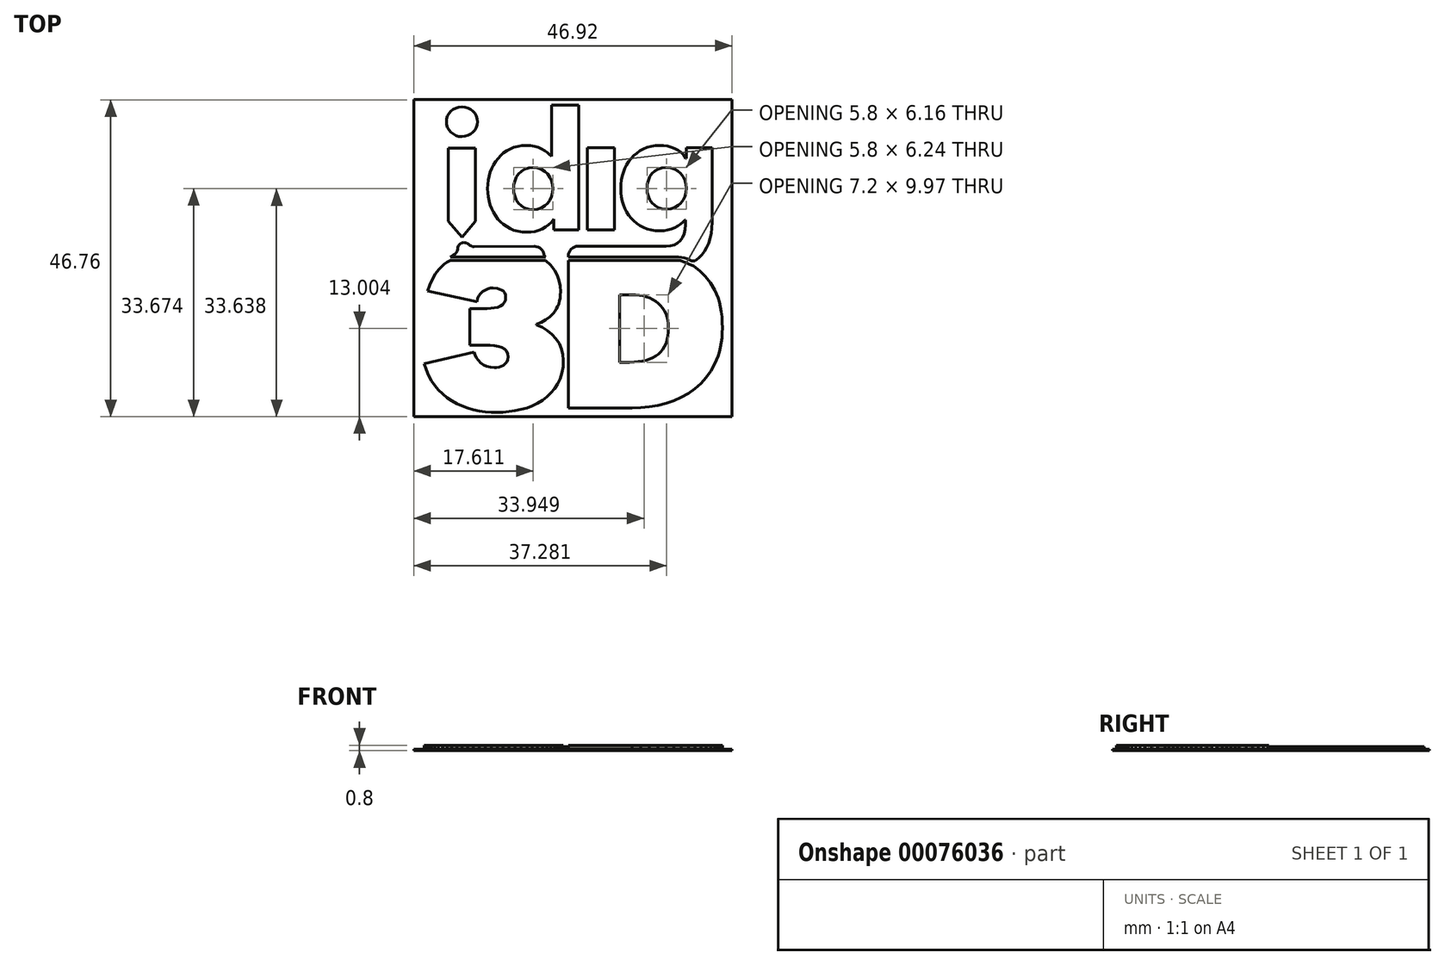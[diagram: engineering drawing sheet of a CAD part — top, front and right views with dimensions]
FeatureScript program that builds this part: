
annotation { "Feature Type Name" : "Feature", "Feature Type Description" : "" }
export const myFeature = defineFeature(function(context is Context, id is Id, definition is map)
    precondition{}
    {
        {
            var Q0;
            Q0=qCreatedBy(makeId("Top.planeOp"),FACE);
            var sketch = newSketch(context, id + "F0", { "sketchPlane" : qUnion([Q0])});
            skLineSegment(sketch, "E0", {"start": v(-3.12, 22.59) * mm, "end": v(0.88, 22.59) * mm});
            skLineSegment(sketch, "E1", {"start": v(0.88, 22.59) * mm, "end": v(0.88, 4.17) * mm});
            skLineSegment(sketch, "E2", {"start": v(17.03, -19.95) * mm, "end": v(16, -20.53) * mm});
            skLineSegment(sketch, "E3", {"start": v(12.5, -21.71) * mm, "end": v(11.27, -21.93) * mm});
            skLineSegment(sketch, "E4", {"start": v(14.9, -21.01) * mm, "end": v(13.73, -21.4) * mm});
            skLineSegment(sketch, "E5", {"start": v(-0.67, -22.1) * mm, "end": v(8.7, -22.1) * mm});
            skLineSegment(sketch, "E6", {"start": v(-3.17, 15) * mm, "end": v(-3.12, 22.59) * mm});
            skLineSegment(sketch, "E7", {"start": v(10, -22.06) * mm, "end": v(8.7, -22.1) * mm});
            skLineSegment(sketch, "E8", {"start": v(17.99, -19.28) * mm, "end": v(17.03, -19.95) * mm});
            skLineSegment(sketch, "E9", {"start": v(-21.3, -17.31) * mm, "end": v(-21.64, -16.47) * mm});
            skLineSegment(sketch, "E10", {"start": v(16, -20.53) * mm, "end": v(14.9, -21.01) * mm});
            skLineSegment(sketch, "E11", {"start": v(13.73, -21.4) * mm, "end": v(12.5, -21.71) * mm});
            skLineSegment(sketch, "E12", {"start": v(11.27, -21.93) * mm, "end": v(10, -22.06) * mm});
            skLineSegment(sketch, "E13", {"start": v(19.65, -17.64) * mm, "end": v(18.86, -18.5) * mm});
            skLineSegment(sketch, "E14", {"start": v(-18.56, -20.57) * mm, "end": v(-19.21, -20.04) * mm});
            skLineSegment(sketch, "E15", {"start": v(-16.35, -21.82) * mm, "end": v(-17.13, -21.46) * mm});
            skLineSegment(sketch, "E16", {"start": v(-11.18, -22.76) * mm, "end": v(-12.07, -22.74) * mm});
            skLineSegment(sketch, "E17", {"start": v(-9.4, -22.65) * mm, "end": v(-10.29, -22.73) * mm});
            skLineSegment(sketch, "E18", {"start": v(-7.64, -22.33) * mm, "end": v(-8.52, -22.52) * mm});
            skLineSegment(sketch, "E19", {"start": v(-15.54, -22.11) * mm, "end": v(-16.35, -21.82) * mm});
            skLineSegment(sketch, "E20", {"start": v(-0.67, -22.1) * mm, "end": v(-0.67, -0.31) * mm});
            skLineSegment(sketch, "E21", {"start": v(-10.29, -22.73) * mm, "end": v(-11.18, -22.76) * mm});
            skLineSegment(sketch, "E22", {"start": v(-5.98, -21.78) * mm, "end": v(-6.8, -22.09) * mm});
            skLineSegment(sketch, "E23", {"start": v(21.43, -14.42) * mm, "end": v(21.2, -15.02) * mm});
            skLineSegment(sketch, "E24", {"start": v(20.94, -15.6) * mm, "end": v(20.34, -16.67) * mm});
            skLineSegment(sketch, "E25", {"start": v(-14.7, -22.35) * mm, "end": v(-15.54, -22.11) * mm});
            skLineSegment(sketch, "E26", {"start": v(21.9, -12.46) * mm, "end": v(21.77, -13.14) * mm});
            skLineSegment(sketch, "E27", {"start": v(-20.38, -18.8) * mm, "end": v(-20.87, -18.09) * mm});
            skLineSegment(sketch, "E28", {"start": v(21.4, -5.87) * mm, "end": v(21.6, -6.52) * mm});
            skLineSegment(sketch, "E29", {"start": v(21.89, -7.91) * mm, "end": v(21.98, -8.66) * mm});
            skLineSegment(sketch, "E30", {"start": v(22.03, -9.45) * mm, "end": v(22.05, -10.28) * mm});
            skLineSegment(sketch, "E31", {"start": v(-21.64, -16.47) * mm, "end": v(-21.91, -15.56) * mm});
            skLineSegment(sketch, "E32", {"start": v(-21.91, -15.56) * mm, "end": v(-14.58, -13.84) * mm});
            skLineSegment(sketch, "E33", {"start": v(21.2, -15.02) * mm, "end": v(20.94, -15.6) * mm});
            skLineSegment(sketch, "E34", {"start": v(-6.8, -22.09) * mm, "end": v(-7.64, -22.33) * mm});
            skLineSegment(sketch, "E35", {"start": v(-13.82, -22.53) * mm, "end": v(-14.7, -22.35) * mm});
            skLineSegment(sketch, "E36", {"start": v(20.34, -16.67) * mm, "end": v(19.65, -17.64) * mm});
            skLineSegment(sketch, "E37", {"start": v(-8.52, -22.52) * mm, "end": v(-9.4, -22.65) * mm});
            skLineSegment(sketch, "E38", {"start": v(-19.21, -20.04) * mm, "end": v(-19.82, -19.45) * mm});
            skLineSegment(sketch, "E39", {"start": v(22.03, -11.03) * mm, "end": v(21.98, -11.76) * mm});
            skLineSegment(sketch, "E40", {"start": v(21.6, -6.52) * mm, "end": v(21.76, -7.2) * mm});
            skLineSegment(sketch, "E41", {"start": v(21.77, -13.14) * mm, "end": v(21.62, -13.8) * mm});
            skLineSegment(sketch, "E42", {"start": v(21.76, -7.2) * mm, "end": v(21.89, -7.91) * mm});
            skLineSegment(sketch, "E43", {"start": v(21.98, -8.66) * mm, "end": v(22.03, -9.45) * mm});
            skLineSegment(sketch, "E44", {"start": v(-20.87, -18.09) * mm, "end": v(-21.3, -17.31) * mm});
            skLineSegment(sketch, "E45", {"start": v(-12.95, -22.66) * mm, "end": v(-13.82, -22.53) * mm});
            skLineSegment(sketch, "E46", {"start": v(-17.87, -21.04) * mm, "end": v(-18.56, -20.57) * mm});
            skLineSegment(sketch, "E47", {"start": v(-3.84, -20.46) * mm, "end": v(-4.5, -20.96) * mm});
            skLineSegment(sketch, "E48", {"start": v(21.62, -13.8) * mm, "end": v(21.43, -14.42) * mm});
            skLineSegment(sketch, "E49", {"start": v(-5.22, -21.4) * mm, "end": v(-5.98, -21.78) * mm});
            skLineSegment(sketch, "E50", {"start": v(21.16, -5.27) * mm, "end": v(21.4, -5.87) * mm});
            skLineSegment(sketch, "E51", {"start": v(-19.82, -19.45) * mm, "end": v(-20.38, -18.8) * mm});
            skLineSegment(sketch, "E52", {"start": v(22.05, -10.28) * mm, "end": v(22.03, -11.03) * mm});
            skLineSegment(sketch, "E53", {"start": v(-12.07, -22.74) * mm, "end": v(-12.95, -22.66) * mm});
            skLineSegment(sketch, "E54", {"start": v(-1.68, -13.4) * mm, "end": v(-1.47, -14.21) * mm});
            skLineSegment(sketch, "E55", {"start": v(13.5, -13.04) * mm, "end": v(13.72, -12.57) * mm});
            skLineSegment(sketch, "E56", {"start": v(-1.4, -15.03) * mm, "end": v(-1.45, -16.02) * mm});
            skLineSegment(sketch, "E57", {"start": v(9.02, -15.34) * mm, "end": v(9.65, -15.29) * mm});
            skLineSegment(sketch, "E58", {"start": v(-1.62, -16.94) * mm, "end": v(-1.88, -17.78) * mm});
            skLineSegment(sketch, "E59", {"start": v(-17.13, -21.46) * mm, "end": v(-17.87, -21.04) * mm});
            skLineSegment(sketch, "E60", {"start": v(13.25, -13.46) * mm, "end": v(13.5, -13.04) * mm});
            skLineSegment(sketch, "E61", {"start": v(6.89, -15.36) * mm, "end": v(8.34, -15.36) * mm});
            skLineSegment(sketch, "E62", {"start": v(10.8, -15.06) * mm, "end": v(11.3, -14.9) * mm});
            skLineSegment(sketch, "E63", {"start": v(-2.26, -18.55) * mm, "end": v(-2.72, -19.25) * mm});
            skLineSegment(sketch, "E64", {"start": v(6.89, -5.39) * mm, "end": v(6.89, -15.36) * mm});
            skLineSegment(sketch, "E65", {"start": v(-3.25, -19.89) * mm, "end": v(-3.84, -20.46) * mm});
            skLineSegment(sketch, "E66", {"start": v(18.86, -18.5) * mm, "end": v(17.99, -19.28) * mm});
            skLineSegment(sketch, "E67", {"start": v(21.98, -11.76) * mm, "end": v(21.9, -12.46) * mm});
            skLineSegment(sketch, "E68", {"start": v(-4.5, -20.96) * mm, "end": v(-5.22, -21.4) * mm});
            skLineSegment(sketch, "E69", {"start": v(-1.98, -6.33) * mm, "end": v(-2.1, -6.74) * mm});
            skLineSegment(sketch, "E70", {"start": v(-14.75, 21.7) * mm, "end": v(-14.47, 21.38) * mm});
            skLineSegment(sketch, "E71", {"start": v(13.88, -12.05) * mm, "end": v(14, -11.49) * mm});
            skLineSegment(sketch, "E72", {"start": v(-18, 21.67) * mm, "end": v(-17.66, 21.94) * mm});
            skLineSegment(sketch, "E73", {"start": v(-17.27, 22.15) * mm, "end": v(-16.84, 22.28) * mm});
            skLineSegment(sketch, "E74", {"start": v(-2.72, -19.25) * mm, "end": v(-3.25, -19.89) * mm});
            skLineSegment(sketch, "E75", {"start": v(12.21, -14.44) * mm, "end": v(12.6, -14.16) * mm});
            skLineSegment(sketch, "E76", {"start": v(9.65, -15.29) * mm, "end": v(10.24, -15.2) * mm});
            skLineSegment(sketch, "E77", {"start": v(10.24, -15.2) * mm, "end": v(10.8, -15.06) * mm});
            skLineSegment(sketch, "E78", {"start": v(11.3, -14.9) * mm, "end": v(11.78, -14.69) * mm});
            skLineSegment(sketch, "E79", {"start": v(11.78, -14.69) * mm, "end": v(12.21, -14.44) * mm});
            skLineSegment(sketch, "E80", {"start": v(12.22, -6.36) * mm, "end": v(11.8, -6.1) * mm});
            skLineSegment(sketch, "E81", {"start": v(13.25, -7.36) * mm, "end": v(12.95, -7) * mm});
            skLineSegment(sketch, "E82", {"start": v(-18.66, 20.14) * mm, "end": v(-18.61, 20.57) * mm});
            skLineSegment(sketch, "E83", {"start": v(13.72, -12.57) * mm, "end": v(13.88, -12.05) * mm});
            skLineSegment(sketch, "E84", {"start": v(10.36, -5.57) * mm, "end": v(9.82, -5.47) * mm});
            skLineSegment(sketch, "E85", {"start": v(14.07, -10.87) * mm, "end": v(14.09, -10.21) * mm});
            skLineSegment(sketch, "E86", {"start": v(-15.91, 22.29) * mm, "end": v(-15.48, 22.16) * mm});
            skLineSegment(sketch, "E87", {"start": v(-1.88, -17.78) * mm, "end": v(-2.26, -18.55) * mm});
            skLineSegment(sketch, "E88", {"start": v(-17.26, 18.1) * mm, "end": v(-17.65, 18.3) * mm});
            skLineSegment(sketch, "E89", {"start": v(-16.84, 17.98) * mm, "end": v(-17.26, 18.1) * mm});
            skLineSegment(sketch, "E90", {"start": v(14.09, -10.21) * mm, "end": v(14.07, -9.66) * mm});
            skLineSegment(sketch, "E91", {"start": v(-14.26, 21) * mm, "end": v(-14.12, 20.58) * mm});
            skLineSegment(sketch, "E92", {"start": v(-18.28, 21.35) * mm, "end": v(-18, 21.67) * mm});
            skLineSegment(sketch, "E93", {"start": v(12.6, -14.16) * mm, "end": v(12.95, -13.83) * mm});
            skLineSegment(sketch, "E94", {"start": v(8.64, -5.39) * mm, "end": v(6.89, -5.39) * mm});
            skLineSegment(sketch, "E95", {"start": v(-14.37, 16.26) * mm, "end": v(-14.37, 5.44) * mm});
            skLineSegment(sketch, "E96", {"start": v(-18.36, 16.26) * mm, "end": v(-14.37, 16.26) * mm});
            skLineSegment(sketch, "E97", {"start": v(-18.36, 5.44) * mm, "end": v(-18.36, 16.26) * mm});
            skLineSegment(sketch, "E98", {"start": v(20.52, 16.3) * mm, "end": v(20.52, 5.31) * mm});
            skLineSegment(sketch, "E99", {"start": v(13.88, -8.64) * mm, "end": v(13.72, -8.18) * mm});
            skLineSegment(sketch, "E100", {"start": v(-21.45, -4.86) * mm, "end": v(-21.12, -3.94) * mm});
            skLineSegment(sketch, "E101", {"start": v(-14.15, -6.41) * mm, "end": v(-21.45, -4.86) * mm});
            skLineSegment(sketch, "E102", {"start": v(8.34, -15.36) * mm, "end": v(9.02, -15.34) * mm});
            skLineSegment(sketch, "E103", {"start": v(-14.08, 20.14) * mm, "end": v(-14.12, 19.69) * mm});
            skLineSegment(sketch, "E104", {"start": v(12.95, -13.83) * mm, "end": v(13.25, -13.46) * mm});
            skLineSegment(sketch, "E105", {"start": v(11.8, -6.1) * mm, "end": v(11.35, -5.89) * mm});
            skLineSegment(sketch, "E106", {"start": v(-16.37, 22.33) * mm, "end": v(-15.91, 22.29) * mm});
            skLineSegment(sketch, "E107", {"start": v(14.07, -9.66) * mm, "end": v(14, -9.13) * mm});
            skLineSegment(sketch, "E108", {"start": v(14, -9.13) * mm, "end": v(13.88, -8.64) * mm});
            skLineSegment(sketch, "E109", {"start": v(-16.37, 17.94) * mm, "end": v(-16.84, 17.98) * mm});
            skLineSegment(sketch, "E110", {"start": v(-15.91, 17.99) * mm, "end": v(-16.37, 17.94) * mm});
            skLineSegment(sketch, "E111", {"start": v(16.75, 16.3) * mm, "end": v(20.52, 16.3) * mm});
            skLineSegment(sketch, "E112", {"start": v(-18, 18.59) * mm, "end": v(-18.29, 18.93) * mm});
            skLineSegment(sketch, "E113", {"start": v(-18.49, 20.98) * mm, "end": v(-18.28, 21.35) * mm});
            skLineSegment(sketch, "E114", {"start": v(-14.12, 20.58) * mm, "end": v(-14.08, 20.14) * mm});
            skLineSegment(sketch, "E115", {"start": v(-18.61, 19.7) * mm, "end": v(-18.66, 20.14) * mm});
            skLineSegment(sketch, "E116", {"start": v(14, -11.49) * mm, "end": v(14.07, -10.87) * mm});
            skLineSegment(sketch, "E117", {"start": v(-9.6, -15) * mm, "end": v(-9.56, -14.57) * mm});
            skLineSegment(sketch, "E118", {"start": v(-10.57, -15.97) * mm, "end": v(-10.25, -15.8) * mm});
            skLineSegment(sketch, "E119", {"start": v(-10.48, -13.18) * mm, "end": v(-10.99, -13.04) * mm});
            skLineSegment(sketch, "E120", {"start": v(-13.6, -15.43) * mm, "end": v(-13.19, -15.75) * mm});
            skLineSegment(sketch, "E121", {"start": v(-2.5, -11.9) * mm, "end": v(-2.02, -12.62) * mm});
            skLineSegment(sketch, "E122", {"start": v(-12.2, 12.7) * mm, "end": v(-11.97, 13.27) * mm});
            skLineSegment(sketch, "E123", {"start": v(-3.76, -10.67) * mm, "end": v(-3.07, -11.24) * mm});
            skLineSegment(sketch, "E124", {"start": v(10.87, -5.7) * mm, "end": v(10.36, -5.57) * mm});
            skLineSegment(sketch, "E125", {"start": v(-1.45, -16.02) * mm, "end": v(-1.62, -16.94) * mm});
            skLineSegment(sketch, "E126", {"start": v(-14.44, -14.27) * mm, "end": v(-14.24, -14.67) * mm});
            skLineSegment(sketch, "E127", {"start": v(-10.99, -13.04) * mm, "end": v(-11.57, -12.94) * mm});
            skLineSegment(sketch, "E128", {"start": v(-1.47, -14.21) * mm, "end": v(-1.4, -15.03) * mm});
            skLineSegment(sketch, "E129", {"start": v(12.95, -7) * mm, "end": v(12.6, -6.66) * mm});
            skLineSegment(sketch, "E130", {"start": v(-16.84, 22.28) * mm, "end": v(-16.37, 22.33) * mm});
            skLineSegment(sketch, "E131", {"start": v(-11.97, 13.27) * mm, "end": v(-11.7, 13.8) * mm});
            skLineSegment(sketch, "E132", {"start": v(13.72, -8.18) * mm, "end": v(13.5, -7.76) * mm});
            skLineSegment(sketch, "E133", {"start": v(-12.96, -12.85) * mm, "end": v(-15.2, -12.85) * mm});
            skLineSegment(sketch, "E134", {"start": v(-15.2, -12.85) * mm, "end": v(-15.2, -7.44) * mm});
            skLineSegment(sketch, "E135", {"start": v(-15.48, 18.11) * mm, "end": v(-15.91, 17.99) * mm});
            skLineSegment(sketch, "E136", {"start": v(-17.66, 21.94) * mm, "end": v(-17.27, 22.15) * mm});
            skLineSegment(sketch, "E137", {"start": v(-17.65, 18.3) * mm, "end": v(-18, 18.59) * mm});
            skLineSegment(sketch, "E138", {"start": v(-14.47, 18.9) * mm, "end": v(-14.75, 18.58) * mm});
            skLineSegment(sketch, "E139", {"start": v(-14.26, 19.27) * mm, "end": v(-14.47, 18.9) * mm});
            skLineSegment(sketch, "E140", {"start": v(-18.5, 19.3) * mm, "end": v(-18.61, 19.7) * mm});
            skLineSegment(sketch, "E141", {"start": v(-10.08, -13.4) * mm, "end": v(-10.48, -13.18) * mm});
            skLineSegment(sketch, "E142", {"start": v(-10.66, 15.16) * mm, "end": v(-10.23, 15.53) * mm});
            skLineSegment(sketch, "E143", {"start": v(-6.54, 13.3) * mm, "end": v(-7.12, 13.1) * mm});
            skLineSegment(sketch, "E144", {"start": v(-9.76, 15.85) * mm, "end": v(-9.25, 16.13) * mm});
            skLineSegment(sketch, "E145", {"start": v(-8.7, 16.35) * mm, "end": v(-8.12, 16.51) * mm});
            skLineSegment(sketch, "E146", {"start": v(-21.12, -3.94) * mm, "end": v(-20.73, -3.1) * mm});
            skLineSegment(sketch, "E147", {"start": v(16.75, 14.74) * mm, "end": v(16.75, 16.3) * mm});
            skLineSegment(sketch, "E148", {"start": v(-3.74, 12.4) * mm, "end": v(-4.16, 12.8) * mm});
            skLineSegment(sketch, "E149", {"start": v(11.35, -5.89) * mm, "end": v(10.87, -5.7) * mm});
            skLineSegment(sketch, "E150", {"start": v(-12.19, -16.11) * mm, "end": v(-11.6, -16.16) * mm});
            skLineSegment(sketch, "E151", {"start": v(-9.62, -14.09) * mm, "end": v(-9.8, -13.7) * mm});
            skLineSegment(sketch, "E152", {"start": v(-9.98, -15.6) * mm, "end": v(-9.76, -15.33) * mm});
            skLineSegment(sketch, "E153", {"start": v(13.94, 16.53) * mm, "end": v(14.49, 16.38) * mm});
            skLineSegment(sketch, "E154", {"start": v(-12.22, -12.87) * mm, "end": v(-12.96, -12.85) * mm});
            skLineSegment(sketch, "E155", {"start": v(10.94, 16.35) * mm, "end": v(11.53, 16.51) * mm});
            skLineSegment(sketch, "E156", {"start": v(-14.24, -14.67) * mm, "end": v(-13.96, -15.06) * mm});
            skLineSegment(sketch, "E157", {"start": v(-14.47, 21.38) * mm, "end": v(-14.26, 21) * mm});
            skLineSegment(sketch, "E158", {"start": v(-3.17, 15) * mm, "end": v(-3.17, 15) * mm});
            skLineSegment(sketch, "E159", {"start": v(-4.6, 16.13) * mm, "end": v(-4.17, 15.87) * mm});
            skLineSegment(sketch, "E160", {"start": v(2.14, 4.17) * mm, "end": v(2.14, 16.3) * mm});
            skLineSegment(sketch, "E161", {"start": v(-12.5, 11.52) * mm, "end": v(-12.37, 12.12) * mm});
            skLineSegment(sketch, "E162", {"start": v(-3.07, -11.24) * mm, "end": v(-2.5, -11.9) * mm});
            skLineSegment(sketch, "E163", {"start": v(6.14, 16.3) * mm, "end": v(6.14, 4.17) * mm});
            skLineSegment(sketch, "E164", {"start": v(-11.7, 13.8) * mm, "end": v(-11.4, 14.29) * mm});
            skLineSegment(sketch, "E165", {"start": v(12.6, -6.66) * mm, "end": v(12.22, -6.36) * mm});
            skLineSegment(sketch, "E166", {"start": v(-10.23, 15.53) * mm, "end": v(-9.76, 15.85) * mm});
            skLineSegment(sketch, "E167", {"start": v(-14.75, 18.58) * mm, "end": v(-15.08, 18.32) * mm});
            skLineSegment(sketch, "E168", {"start": v(9.87, 15.83) * mm, "end": v(10.39, 16.12) * mm});
            skLineSegment(sketch, "E169", {"start": v(13.5, -7.76) * mm, "end": v(13.25, -7.36) * mm});
            skLineSegment(sketch, "E170", {"start": v(-2.02, -12.62) * mm, "end": v(-1.68, -13.4) * mm});
            skLineSegment(sketch, "E171", {"start": v(-14.12, 19.69) * mm, "end": v(-14.26, 19.27) * mm});
            skLineSegment(sketch, "E172", {"start": v(-18.29, 18.93) * mm, "end": v(-18.5, 19.3) * mm});
            skLineSegment(sketch, "E173", {"start": v(-5.87, 13.38) * mm, "end": v(-6.54, 13.3) * mm});
            skLineSegment(sketch, "E174", {"start": v(-18.61, 20.57) * mm, "end": v(-18.49, 20.98) * mm});
            skLineSegment(sketch, "E175", {"start": v(-14.58, -13.84) * mm, "end": v(-14.44, -14.27) * mm});
            skLineSegment(sketch, "E176", {"start": v(-15.23, 1.9) * mm, "end": v(-15.03, 1.8) * mm});
            skLineSegment(sketch, "E177", {"start": v(-10.35, -6.88) * mm, "end": v(-10.11, -6.58) * mm});
            skLineSegment(sketch, "E178", {"start": v(-4.16, 7.72) * mm, "end": v(-3.74, 8.11) * mm});
            skLineSegment(sketch, "E179", {"start": v(-8.57, 11.43) * mm, "end": v(-8.7, 10.86) * mm});
            skLineSegment(sketch, "E180", {"start": v(-8.75, 10.28) * mm, "end": v(-8.7, 9.7) * mm});
            skLineSegment(sketch, "E181", {"start": v(-11.73, 6.75) * mm, "end": v(-12, 7.28) * mm});
            skLineSegment(sketch, "E182", {"start": v(-14.37, 5.44) * mm, "end": v(-16.36, 3.12) * mm});
            skLineSegment(sketch, "E183", {"start": v(-15.71, 2.24) * mm, "end": v(-15.55, 2.16) * mm});
            skLineSegment(sketch, "E184", {"start": v(-2.24, -7.12) * mm, "end": v(-2.42, -7.48) * mm});
            skLineSegment(sketch, "E185", {"start": v(8.57, 14.72) * mm, "end": v(8.96, 15.13) * mm});
            skLineSegment(sketch, "E186", {"start": v(12.08, 12.85) * mm, "end": v(11.68, 12.47) * mm});
            skLineSegment(sketch, "E187", {"start": v(-7.12, 13.1) * mm, "end": v(-7.6, 12.8) * mm});
            skLineSegment(sketch, "E188", {"start": v(-9.26, 4.36) * mm, "end": v(-9.78, 4.65) * mm});
            skLineSegment(sketch, "E189", {"start": v(-3.16, 9.11) * mm, "end": v(-3, 9.68) * mm});
            skLineSegment(sketch, "E190", {"start": v(7.65, 13.25) * mm, "end": v(7.92, 13.77) * mm});
            skLineSegment(sketch, "E191", {"start": v(-4.02, -9.1) * mm, "end": v(-4.68, -9.45) * mm});
            skLineSegment(sketch, "E192", {"start": v(-20.73, -3.1) * mm, "end": v(-20.28, -2.33) * mm});
            skLineSegment(sketch, "E193", {"start": v(16.7, 14.74) * mm, "end": v(16.75, 14.74) * mm});
            skLineSegment(sketch, "E194", {"start": v(-12.57, 9.65) * mm, "end": v(-12.6, 10.28) * mm});
            skLineSegment(sketch, "E195", {"start": v(-5.64, 16.51) * mm, "end": v(-5.1, 16.35) * mm});
            skLineSegment(sketch, "E196", {"start": v(-4.54, -10.2) * mm, "end": v(-3.76, -10.67) * mm});
            skLineSegment(sketch, "E197", {"start": v(-12.18, -4.43) * mm, "end": v(-12.56, -4.53) * mm});
            skLineSegment(sketch, "E198", {"start": v(7.44, 12.7) * mm, "end": v(7.65, 13.25) * mm});
            skLineSegment(sketch, "E199", {"start": v(-3, 10.84) * mm, "end": v(-3.16, 11.4) * mm});
            skLineSegment(sketch, "E200", {"start": v(-3.74, 8.11) * mm, "end": v(-3.4, 8.58) * mm});
            skLineSegment(sketch, "E201", {"start": v(-10.11, -6.58) * mm, "end": v(-9.97, -6.2) * mm});
            skLineSegment(sketch, "E202", {"start": v(-8.02, 8.11) * mm, "end": v(-7.6, 7.72) * mm});
            skLineSegment(sketch, "E203", {"start": v(-12.72, -15.97) * mm, "end": v(-12.19, -16.11) * mm});
            skLineSegment(sketch, "E204", {"start": v(-8.7, 9.7) * mm, "end": v(-8.57, 9.12) * mm});
            skLineSegment(sketch, "E205", {"start": v(-19.76, -1.64) * mm, "end": v(-19.4, -1.26) * mm});
            skLineSegment(sketch, "E206", {"start": v(-17.6, 0.47) * mm, "end": v(-17.35, 0.65) * mm});
            skLineSegment(sketch, "E207", {"start": v(-2.63, -7.8) * mm, "end": v(-2.87, -8.11) * mm});
            skLineSegment(sketch, "E208", {"start": v(15.92, 12.46) * mm, "end": v(15.5, 12.84) * mm});
            skLineSegment(sketch, "E209", {"start": v(-11.57, -12.94) * mm, "end": v(-12.22, -12.87) * mm});
            skLineSegment(sketch, "E210", {"start": v(-16.36, 3.12) * mm, "end": v(-18.36, 5.44) * mm});
            skLineSegment(sketch, "E211", {"start": v(-3.78, 15.6) * mm, "end": v(-3.45, 15.3) * mm});
            skLineSegment(sketch, "E212", {"start": v(-5.23, 13.3) * mm, "end": v(-5.87, 13.38) * mm});
            skLineSegment(sketch, "E213", {"start": v(15.51, 15.92) * mm, "end": v(15.96, 15.59) * mm});
            skLineSegment(sketch, "E214", {"start": v(-15.2, -7.44) * mm, "end": v(-12.7, -7.44) * mm});
            skLineSegment(sketch, "E215", {"start": v(-8.02, 12.41) * mm, "end": v(-8.34, 11.95) * mm});
            skLineSegment(sketch, "E216", {"start": v(-5.1, 16.35) * mm, "end": v(-4.6, 16.13) * mm});
            skLineSegment(sketch, "E217", {"start": v(-10.25, -15.8) * mm, "end": v(-9.98, -15.6) * mm});
            skLineSegment(sketch, "E218", {"start": v(-9.56, -14.57) * mm, "end": v(-9.62, -14.09) * mm});
            skLineSegment(sketch, "E219", {"start": v(-14.59, 1.7) * mm, "end": v(-5.68, 1.73) * mm});
            skLineSegment(sketch, "E220", {"start": v(-2.1, -6.74) * mm, "end": v(-2.24, -7.12) * mm});
            skLineSegment(sketch, "E221", {"start": v(12.82, 16.64) * mm, "end": v(13.39, 16.61) * mm});
            skLineSegment(sketch, "E222", {"start": v(-15.48, 22.16) * mm, "end": v(-15.08, 21.96) * mm});
            skLineSegment(sketch, "E223", {"start": v(-10.25, 4.99) * mm, "end": v(-10.68, 5.36) * mm});
            skLineSegment(sketch, "E224", {"start": v(-4, 0.16) * mm, "end": v(-18.09, 0.16) * mm});
            skLineSegment(sketch, "E225", {"start": v(-9.25, 16.13) * mm, "end": v(-8.7, 16.35) * mm});
            skLineSegment(sketch, "E226", {"start": v(2.14, 16.3) * mm, "end": v(6.14, 16.3) * mm});
            skLineSegment(sketch, "E227", {"start": v(-11.13, -4.47) * mm, "end": v(-11.77, -4.4) * mm});
            skLineSegment(sketch, "E228", {"start": v(-12.56, -4.53) * mm, "end": v(-12.94, -4.69) * mm});
            skLineSegment(sketch, "E229", {"start": v(-12.1, -7.42) * mm, "end": v(-11.57, -7.35) * mm});
            skLineSegment(sketch, "E230", {"start": v(-15.08, 18.32) * mm, "end": v(-15.48, 18.11) * mm});
            skLineSegment(sketch, "E231", {"start": v(-13.96, -15.06) * mm, "end": v(-13.6, -15.43) * mm});
            skLineSegment(sketch, "E232", {"start": v(-11.4, 14.29) * mm, "end": v(-11.05, 14.74) * mm});
            skLineSegment(sketch, "E233", {"start": v(-12.37, 12.12) * mm, "end": v(-12.2, 12.7) * mm});
            skLineSegment(sketch, "E234", {"start": v(9.4, 15.5) * mm, "end": v(9.87, 15.83) * mm});
            skLineSegment(sketch, "E235", {"start": v(-18.56, -0.61) * mm, "end": v(-18.09, -0.31) * mm});
            skLineSegment(sketch, "E236", {"start": v(-12.5, 9.04) * mm, "end": v(-12.57, 9.65) * mm});
            skLineSegment(sketch, "E237", {"start": v(-3.42, -8.65) * mm, "end": v(-4.02, -9.1) * mm});
            skLineSegment(sketch, "E238", {"start": v(-8.7, 10.86) * mm, "end": v(-8.75, 10.28) * mm});
            skLineSegment(sketch, "E239", {"start": v(9.82, -5.47) * mm, "end": v(9.24, -5.4) * mm});
            skLineSegment(sketch, "E240", {"start": v(-1.85, -5.44) * mm, "end": v(-1.9, -5.9) * mm});
            skLineSegment(sketch, "E241", {"start": v(-10.68, -7.09) * mm, "end": v(-10.35, -6.88) * mm});
            skLineSegment(sketch, "E242", {"start": v(-3, 9.68) * mm, "end": v(-2.95, 10.26) * mm});
            skLineSegment(sketch, "E243", {"start": v(-12.57, 10.9) * mm, "end": v(-12.5, 11.52) * mm});
            skLineSegment(sketch, "E244", {"start": v(19.54, -2.7) * mm, "end": v(20.27, -3.64) * mm});
            skLineSegment(sketch, "E245", {"start": v(-17.02, 1.36) * mm, "end": v(-17, 1.56) * mm});
            skLineSegment(sketch, "E246", {"start": v(-5.4, -9.72) * mm, "end": v(-5.4, -9.85) * mm});
            skLineSegment(sketch, "E247", {"start": v(-7.6, 12.8) * mm, "end": v(-8.02, 12.41) * mm});
            skLineSegment(sketch, "E248", {"start": v(-15.41, 2.05) * mm, "end": v(-15.23, 1.9) * mm});
            skLineSegment(sketch, "E249", {"start": v(11.68, 12.47) * mm, "end": v(11.35, 12.02) * mm});
            skLineSegment(sketch, "E250", {"start": v(-10.52, -4.7) * mm, "end": v(-11.13, -4.47) * mm});
            skLineSegment(sketch, "E251", {"start": v(7.27, 12.11) * mm, "end": v(7.44, 12.7) * mm});
            skLineSegment(sketch, "E252", {"start": v(20.9, -4.7) * mm, "end": v(21.16, -5.27) * mm});
            skLineSegment(sketch, "E253", {"start": v(-10.91, -16.07) * mm, "end": v(-10.57, -15.97) * mm});
            skLineSegment(sketch, "E254", {"start": v(-7.6, 7.72) * mm, "end": v(-7.12, 7.4) * mm});
            skLineSegment(sketch, "E255", {"start": v(-4.16, 12.8) * mm, "end": v(-4.66, 13.1) * mm});
            skLineSegment(sketch, "E256", {"start": v(-17.35, 0.65) * mm, "end": v(-17.17, 0.84) * mm});
            skLineSegment(sketch, "E257", {"start": v(7.92, 13.77) * mm, "end": v(8.22, 14.26) * mm});
            skLineSegment(sketch, "E258", {"start": v(15.5, 12.84) * mm, "end": v(15, 13.13) * mm});
            skLineSegment(sketch, "E259", {"start": v(14.49, 16.38) * mm, "end": v(15.02, 16.18) * mm});
            skLineSegment(sketch, "E260", {"start": v(-19, -0.93) * mm, "end": v(-18.56, -0.61) * mm});
            skLineSegment(sketch, "E261", {"start": v(-12.2, 7.85) * mm, "end": v(-12.38, 8.44) * mm});
            skLineSegment(sketch, "E262", {"start": v(-9.76, -15.33) * mm, "end": v(-9.6, -15) * mm});
            skLineSegment(sketch, "E263", {"start": v(-5.23, 7.2) * mm, "end": v(-4.66, 7.4) * mm});
            skLineSegment(sketch, "E264", {"start": v(15.96, 15.59) * mm, "end": v(16.35, 15.2) * mm});
            skLineSegment(sketch, "E265", {"start": v(-3.16, 11.4) * mm, "end": v(-3.4, 11.93) * mm});
            skLineSegment(sketch, "E266", {"start": v(-2.42, -7.48) * mm, "end": v(-2.63, -7.8) * mm});
            skLineSegment(sketch, "E267", {"start": v(-8.57, 9.12) * mm, "end": v(-8.34, 8.59) * mm});
            skLineSegment(sketch, "E268", {"start": v(-18.09, -0.31) * mm, "end": v(-4, -0.31) * mm});
            skLineSegment(sketch, "E269", {"start": v(-9.78, 4.65) * mm, "end": v(-10.25, 4.99) * mm});
            skLineSegment(sketch, "E270", {"start": v(10.39, 16.12) * mm, "end": v(10.94, 16.35) * mm});
            skLineSegment(sketch, "E271", {"start": v(-20.28, -2.33) * mm, "end": v(-19.76, -1.64) * mm});
            skLineSegment(sketch, "E272", {"start": v(-15.08, 21.96) * mm, "end": v(-14.75, 21.7) * mm});
            skLineSegment(sketch, "E273", {"start": v(-8.12, 16.51) * mm, "end": v(-7.51, 16.6) * mm});
            skLineSegment(sketch, "E274", {"start": v(-14.03, -5.95) * mm, "end": v(-14.15, -6.41) * mm});
            skLineSegment(sketch, "E275", {"start": v(-12.94, -4.69) * mm, "end": v(-13.3, -4.91) * mm});
            skLineSegment(sketch, "E276", {"start": v(-11.08, 5.79) * mm, "end": v(-11.42, 6.25) * mm});
            skLineSegment(sketch, "E277", {"start": v(-11.42, 6.25) * mm, "end": v(-11.73, 6.75) * mm});
            skLineSegment(sketch, "E278", {"start": v(-8.34, 11.95) * mm, "end": v(-8.57, 11.43) * mm});
            skLineSegment(sketch, "E279", {"start": v(-11.05, 14.74) * mm, "end": v(-10.66, 15.16) * mm});
            skLineSegment(sketch, "E280", {"start": v(-3.45, 15.3) * mm, "end": v(-3.17, 15) * mm});
            skLineSegment(sketch, "E281", {"start": v(-9.8, -13.7) * mm, "end": v(-10.08, -13.4) * mm});
            skLineSegment(sketch, "E282", {"start": v(-4.17, 15.87) * mm, "end": v(-3.78, 15.6) * mm});
            skLineSegment(sketch, "E283", {"start": v(-12.38, 8.44) * mm, "end": v(-12.5, 9.04) * mm});
            skLineSegment(sketch, "E284", {"start": v(-11.1, -7.24) * mm, "end": v(-10.68, -7.09) * mm});
            skLineSegment(sketch, "E285", {"start": v(16.72, 10.3) * mm, "end": v(16.67, 10.9) * mm});
            skLineSegment(sketch, "E286", {"start": v(-12.6, 10.28) * mm, "end": v(-12.57, 10.9) * mm});
            skLineSegment(sketch, "E287", {"start": v(9.24, -5.4) * mm, "end": v(8.64, -5.39) * mm});
            skLineSegment(sketch, "E288", {"start": v(-16.07, 2.31) * mm, "end": v(-15.89, 2.3) * mm});
            skLineSegment(sketch, "E289", {"start": v(-4.68, -9.45) * mm, "end": v(-5.4, -9.72) * mm});
            skLineSegment(sketch, "E290", {"start": v(-10.26, -4.87) * mm, "end": v(-10.52, -4.7) * mm});
            skLineSegment(sketch, "E291", {"start": v(11.35, 12.02) * mm, "end": v(11.12, 11.5) * mm});
            skLineSegment(sketch, "E292", {"start": v(15.02, 16.18) * mm, "end": v(15.51, 15.92) * mm});
            skLineSegment(sketch, "E293", {"start": v(7.15, 11.52) * mm, "end": v(7.27, 12.11) * mm});
            skLineSegment(sketch, "E294", {"start": v(-11.6, -16.16) * mm, "end": v(-11.27, -16.14) * mm});
            skLineSegment(sketch, "E295", {"start": v(-18.09, 0.16) * mm, "end": v(-17.6, 0.47) * mm});
            skLineSegment(sketch, "E296", {"start": v(13.13, 13.32) * mm, "end": v(12.57, 13.13) * mm});
            skLineSegment(sketch, "E297", {"start": v(-7.12, 7.4) * mm, "end": v(-6.54, 7.2) * mm});
            skLineSegment(sketch, "E298", {"start": v(-5.87, 7.14) * mm, "end": v(-5.23, 7.2) * mm});
            skLineSegment(sketch, "E299", {"start": v(8.96, 15.13) * mm, "end": v(9.4, 15.5) * mm});
            skLineSegment(sketch, "E300", {"start": v(-1.9, -5.9) * mm, "end": v(-1.98, -6.33) * mm});
            skLineSegment(sketch, "E301", {"start": v(-2.87, -8.11) * mm, "end": v(-3.42, -8.65) * mm});
            skLineSegment(sketch, "E302", {"start": v(14.42, 13.32) * mm, "end": v(13.77, 13.38) * mm});
            skLineSegment(sketch, "E303", {"start": v(16.51, 11.48) * mm, "end": v(16.26, 12) * mm});
            skLineSegment(sketch, "E304", {"start": v(-10.68, 5.36) * mm, "end": v(-11.08, 5.79) * mm});
            skLineSegment(sketch, "E305", {"start": v(7.07, 10.9) * mm, "end": v(7.15, 11.52) * mm});
            skLineSegment(sketch, "E306", {"start": v(-14.81, 1.73) * mm, "end": v(-14.59, 1.7) * mm});
            skLineSegment(sketch, "E307", {"start": v(12.16, 16.6) * mm, "end": v(12.82, 16.64) * mm});
            skLineSegment(sketch, "E308", {"start": v(20.27, -3.64) * mm, "end": v(20.9, -4.7) * mm});
            skLineSegment(sketch, "E309", {"start": v(-3.4, 11.93) * mm, "end": v(-3.74, 12.4) * mm});
            skLineSegment(sketch, "E310", {"start": v(-3.4, 8.58) * mm, "end": v(-3.16, 9.11) * mm});
            skLineSegment(sketch, "E311", {"start": v(-12, 7.28) * mm, "end": v(-12.2, 7.85) * mm});
            skLineSegment(sketch, "E312", {"start": v(-8.7, 4.13) * mm, "end": v(-9.26, 4.36) * mm});
            skLineSegment(sketch, "E313", {"start": v(16.35, 15.2) * mm, "end": v(16.7, 14.74) * mm});
            skLineSegment(sketch, "E314", {"start": v(-19.4, -1.26) * mm, "end": v(-19, -0.93) * mm});
            skLineSegment(sketch, "E315", {"start": v(-13.3, -4.91) * mm, "end": v(-13.6, -5.2) * mm});
            skLineSegment(sketch, "E316", {"start": v(-13.85, -5.54) * mm, "end": v(-14.03, -5.95) * mm});
            skLineSegment(sketch, "E317", {"start": v(-6.23, 16.6) * mm, "end": v(-5.64, 16.51) * mm});
            skLineSegment(sketch, "E318", {"start": v(-8.34, 8.59) * mm, "end": v(-8.02, 8.11) * mm});
            skLineSegment(sketch, "E319", {"start": v(-4.66, 13.1) * mm, "end": v(-5.23, 13.3) * mm});
            skLineSegment(sketch, "E320", {"start": v(-2.95, 10.26) * mm, "end": v(-3, 10.84) * mm});
            skLineSegment(sketch, "E321", {"start": v(-6.87, 16.64) * mm, "end": v(-6.23, 16.6) * mm});
            skLineSegment(sketch, "E322", {"start": v(11.68, 8.15) * mm, "end": v(12.08, 7.77) * mm});
            skLineSegment(sketch, "E323", {"start": v(10.97, 9.7) * mm, "end": v(11.12, 9.14) * mm});
            skLineSegment(sketch, "E324", {"start": v(15.5, 7.76) * mm, "end": v(15.93, 8.14) * mm});
            skLineSegment(sketch, "E325", {"start": v(7.44, 7.88) * mm, "end": v(7.27, 8.46) * mm});
            skLineSegment(sketch, "E326", {"start": v(20.5, 4.45) * mm, "end": v(20.4, 3.65) * mm});
            skLineSegment(sketch, "E327", {"start": v(-16.26, 2.3) * mm, "end": v(-16.07, 2.31) * mm});
            skLineSegment(sketch, "E328", {"start": v(16.67, 10.9) * mm, "end": v(16.51, 11.48) * mm});
            skLineSegment(sketch, "E329", {"start": v(-9.97, -6.2) * mm, "end": v(-9.92, -5.75) * mm});
            skLineSegment(sketch, "E330", {"start": v(-10.07, -5.1) * mm, "end": v(-10.26, -4.87) * mm});
            skLineSegment(sketch, "E331", {"start": v(7.15, 9.05) * mm, "end": v(7.07, 9.66) * mm});
            skLineSegment(sketch, "E332", {"start": v(-5.4, -9.85) * mm, "end": v(-4.54, -10.2) * mm});
            skLineSegment(sketch, "E333", {"start": v(13.39, 16.61) * mm, "end": v(13.94, 16.53) * mm});
            skLineSegment(sketch, "E334", {"start": v(-13.19, -15.75) * mm, "end": v(-12.72, -15.97) * mm});
            skLineSegment(sketch, "E335", {"start": v(-6.54, 7.2) * mm, "end": v(-5.87, 7.14) * mm});
            skLineSegment(sketch, "E336", {"start": v(15, 13.13) * mm, "end": v(14.42, 13.32) * mm});
            skLineSegment(sketch, "E337", {"start": v(16.26, 8.59) * mm, "end": v(16.51, 9.11) * mm});
            skLineSegment(sketch, "E338", {"start": v(8.22, 14.26) * mm, "end": v(8.57, 14.72) * mm});
            skLineSegment(sketch, "E339", {"start": v(10.97, 10.92) * mm, "end": v(10.92, 10.3) * mm});
            skLineSegment(sketch, "E340", {"start": v(-17.06, 1.08) * mm, "end": v(-17.02, 1.36) * mm});
            skLineSegment(sketch, "E341", {"start": v(-4.66, 7.4) * mm, "end": v(-4.16, 7.72) * mm});
            skLineSegment(sketch, "E342", {"start": v(16.51, 9.11) * mm, "end": v(16.67, 9.7) * mm});
            skLineSegment(sketch, "E343", {"start": v(20.23, 2.9) * mm, "end": v(20.01, 2.22) * mm});
            skLineSegment(sketch, "E344", {"start": v(-15.03, 1.8) * mm, "end": v(-14.81, 1.73) * mm});
            skLineSegment(sketch, "E345", {"start": v(11.53, 16.51) * mm, "end": v(12.16, 16.6) * mm});
            skLineSegment(sketch, "E346", {"start": v(12.57, 13.13) * mm, "end": v(12.08, 12.85) * mm});
            skLineSegment(sketch, "E347", {"start": v(-13.6, -5.2) * mm, "end": v(-13.85, -5.54) * mm});
            skLineSegment(sketch, "E348", {"start": v(7.05, 10.28) * mm, "end": v(7.07, 10.9) * mm});
            skLineSegment(sketch, "E349", {"start": v(-7.51, 16.6) * mm, "end": v(-6.87, 16.64) * mm});
            skLineSegment(sketch, "E350", {"start": v(16.26, 12) * mm, "end": v(15.92, 12.46) * mm});
            skLineSegment(sketch, "E351", {"start": v(7.65, 7.33) * mm, "end": v(7.44, 7.88) * mm});
            skLineSegment(sketch, "E352", {"start": v(12.08, 7.77) * mm, "end": v(12.57, 7.47) * mm});
            skLineSegment(sketch, "E353", {"start": v(-15.89, 2.3) * mm, "end": v(-15.71, 2.24) * mm});
            skLineSegment(sketch, "E354", {"start": v(11.12, 9.14) * mm, "end": v(11.35, 8.6) * mm});
            skLineSegment(sketch, "E355", {"start": v(15.93, 8.14) * mm, "end": v(16.26, 8.59) * mm});
            skLineSegment(sketch, "E356", {"start": v(12.57, 7.47) * mm, "end": v(13.13, 7.28) * mm});
            skLineSegment(sketch, "E357", {"start": v(-12.7, -7.44) * mm, "end": v(-12.1, -7.42) * mm});
            skLineSegment(sketch, "E358", {"start": v(-11.27, -16.14) * mm, "end": v(-10.91, -16.07) * mm});
            skLineSegment(sketch, "E359", {"start": v(-9.96, -5.4) * mm, "end": v(-10.07, -5.1) * mm});
            skLineSegment(sketch, "E360", {"start": v(13.77, 13.38) * mm, "end": v(13.13, 13.32) * mm});
            skLineSegment(sketch, "E361", {"start": v(11.12, 11.5) * mm, "end": v(10.97, 10.92) * mm});
            skLineSegment(sketch, "E362", {"start": v(7.27, 8.46) * mm, "end": v(7.15, 9.05) * mm});
            skLineSegment(sketch, "E363", {"start": v(16.67, 9.7) * mm, "end": v(16.72, 10.3) * mm});
            skLineSegment(sketch, "E364", {"start": v(-17.17, 0.84) * mm, "end": v(-17.06, 1.08) * mm});
            skLineSegment(sketch, "E365", {"start": v(-1.88, -4.07) * mm, "end": v(-1.83, -4.96) * mm});
            skLineSegment(sketch, "E366", {"start": v(-16.44, 2.24) * mm, "end": v(-16.26, 2.3) * mm});
            skLineSegment(sketch, "E367", {"start": v(7.92, 6.82) * mm, "end": v(7.65, 7.33) * mm});
            skLineSegment(sketch, "E368", {"start": v(14.42, 7.28) * mm, "end": v(15, 7.47) * mm});
            skLineSegment(sketch, "E369", {"start": v(10.92, 10.3) * mm, "end": v(10.97, 9.7) * mm});
            skLineSegment(sketch, "E370", {"start": v(11.35, 8.6) * mm, "end": v(11.68, 8.15) * mm});
            skLineSegment(sketch, "E371", {"start": v(-11.77, -4.4) * mm, "end": v(-12.18, -4.43) * mm});
            skLineSegment(sketch, "E372", {"start": v(-11.57, -7.35) * mm, "end": v(-11.1, -7.24) * mm});
            skLineSegment(sketch, "E373", {"start": v(7.07, 9.66) * mm, "end": v(7.05, 10.28) * mm});
            skLineSegment(sketch, "E374", {"start": v(-16.6, 2.15) * mm, "end": v(-16.44, 2.24) * mm});
            skLineSegment(sketch, "E375", {"start": v(-1.83, -4.96) * mm, "end": v(-1.85, -5.44) * mm});
            skLineSegment(sketch, "E376", {"start": v(13.13, 7.28) * mm, "end": v(13.77, 7.21) * mm});
            skLineSegment(sketch, "E377", {"start": v(-9.92, -5.75) * mm, "end": v(-9.96, -5.4) * mm});
            skLineSegment(sketch, "E378", {"start": v(8.22, 6.34) * mm, "end": v(7.92, 6.82) * mm});
            skLineSegment(sketch, "E379", {"start": v(-17.02, 1.36) * mm, "end": v(-17.02, 1.36) * mm});
            skLineSegment(sketch, "E380", {"start": v(13.77, 7.21) * mm, "end": v(14.42, 7.28) * mm});
            skLineSegment(sketch, "E381", {"start": v(-2.04, -3.25) * mm, "end": v(-1.88, -4.07) * mm});
            skLineSegment(sketch, "E382", {"start": v(15, 7.47) * mm, "end": v(15.5, 7.76) * mm});
            skLineSegment(sketch, "E383", {"start": v(13.94, 0.16) * mm, "end": v(13.42, 0.16) * mm});
            skLineSegment(sketch, "E384", {"start": v(-0.64, 0.16) * mm, "end": v(-0.68, 0.16) * mm});
            skLineSegment(sketch, "E385", {"start": v(4.34, 1.76) * mm, "end": v(4.86, 1.76) * mm});
            skLineSegment(sketch, "E386", {"start": v(16.03, 0.13) * mm, "end": v(15.6, 0.16) * mm});
            skLineSegment(sketch, "E387", {"start": v(-4.67, 1.32) * mm, "end": v(-4.5, 1.11) * mm});
            skLineSegment(sketch, "E388", {"start": v(14.52, 4.3) * mm, "end": v(14, 4.15) * mm});
            skLineSegment(sketch, "E389", {"start": v(2.43, 1.76) * mm, "end": v(2.87, 1.76) * mm});
            skLineSegment(sketch, "E390", {"start": v(15.81, -0.31) * mm, "end": v(17.8, -1.15) * mm});
            skLineSegment(sketch, "E391", {"start": v(-7.49, 3.86) * mm, "end": v(-8.11, 3.96) * mm});
            skLineSegment(sketch, "E392", {"start": v(19, 0.5) * mm, "end": v(18.57, 0.04) * mm});
            skLineSegment(sketch, "E393", {"start": v(1.4, 0.16) * mm, "end": v(0.94, 0.16) * mm});
            skLineSegment(sketch, "E394", {"start": v(20.4, 3.65) * mm, "end": v(20.23, 2.9) * mm});
            skLineSegment(sketch, "E395", {"start": v(16.6, 4.92) * mm, "end": v(16.6, 5.65) * mm});
            skLineSegment(sketch, "E396", {"start": v(10.79, 1.76) * mm, "end": v(11.25, 1.76) * mm});
            skLineSegment(sketch, "E397", {"start": v(14.94, 1.97) * mm, "end": v(15.43, 2.23) * mm});
            skLineSegment(sketch, "E398", {"start": v(12.17, 4.08) * mm, "end": v(11.54, 4.17) * mm});
            skLineSegment(sketch, "E399", {"start": v(-6.82, 3.82) * mm, "end": v(-7.49, 3.86) * mm});
            skLineSegment(sketch, "E400", {"start": v(-4.01, 4.6) * mm, "end": v(-4.52, 4.32) * mm});
            skLineSegment(sketch, "E401", {"start": v(9.67, 0.16) * mm, "end": v(8.98, 0.16) * mm});
            skLineSegment(sketch, "E402", {"start": v(-0.26, 1.34) * mm, "end": v(-0.04, 1.52) * mm});
            skLineSegment(sketch, "E403", {"start": v(-4, -0.31) * mm, "end": v(-3.3, -1.01) * mm});
            skLineSegment(sketch, "E404", {"start": v(8.74, 1.76) * mm, "end": v(9.27, 1.76) * mm});
            skLineSegment(sketch, "E405", {"start": v(4.22, 0.16) * mm, "end": v(3.6, 0.16) * mm});
            skLineSegment(sketch, "E406", {"start": v(1.9, 0.16) * mm, "end": v(1.4, 0.16) * mm});
            skLineSegment(sketch, "E407", {"start": v(18.72, -1.87) * mm, "end": v(19.54, -2.7) * mm});
            skLineSegment(sketch, "E408", {"start": v(-2.8, 5.75) * mm, "end": v(-2.8, 4.17) * mm});
            skLineSegment(sketch, "E409", {"start": v(-2.31, -2.5) * mm, "end": v(-2.04, -3.25) * mm});
            skLineSegment(sketch, "E410", {"start": v(20.52, 5.31) * mm, "end": v(20.5, 4.45) * mm});
            skLineSegment(sketch, "E411", {"start": v(15.81, -0.31) * mm, "end": v(-0.67, -0.31) * mm});
            skLineSegment(sketch, "E412", {"start": v(17.8, -1.15) * mm, "end": v(18.72, -1.87) * mm});
            skLineSegment(sketch, "E413", {"start": v(9.87, 4.82) * mm, "end": v(9.4, 5.13) * mm});
            skLineSegment(sketch, "E414", {"start": v(0.88, 4.17) * mm, "end": v(-2.8, 4.17) * mm});
            skLineSegment(sketch, "E415", {"start": v(-15.55, 2.16) * mm, "end": v(-15.41, 2.05) * mm});
            skLineSegment(sketch, "E416", {"start": v(6.14, 4.17) * mm, "end": v(2.14, 4.17) * mm});
            skLineSegment(sketch, "E417", {"start": v(16.22, 5.3) * mm, "end": v(15.87, 5) * mm});
            skLineSegment(sketch, "E418", {"start": v(4.86, 0.16) * mm, "end": v(4.22, 0.16) * mm});
            skLineSegment(sketch, "E419", {"start": v(-4.3, 0.63) * mm, "end": v(-4.26, 0.37) * mm});
            skLineSegment(sketch, "E420", {"start": v(-0.35, 0.16) * mm, "end": v(-0.53, 0.16) * mm});
            skLineSegment(sketch, "E421", {"start": v(14.43, 0.16) * mm, "end": v(13.94, 0.16) * mm});
            skLineSegment(sketch, "E422", {"start": v(3.83, 1.76) * mm, "end": v(4.34, 1.76) * mm});
            skLineSegment(sketch, "E423", {"start": v(16.44, 0.05) * mm, "end": v(16.03, 0.13) * mm});
            skLineSegment(sketch, "E424", {"start": v(19.4, 1.01) * mm, "end": v(19, 0.5) * mm});
            skLineSegment(sketch, "E425", {"start": v(-4.89, 1.5) * mm, "end": v(-4.67, 1.32) * mm});
            skLineSegment(sketch, "E426", {"start": v(1.64, 1.76) * mm, "end": v(2.02, 1.76) * mm});
            skLineSegment(sketch, "E427", {"start": v(15.83, 2.58) * mm, "end": v(16.16, 3.03) * mm});
            skLineSegment(sketch, "E428", {"start": v(15.02, 4.48) * mm, "end": v(14.52, 4.3) * mm});
            skLineSegment(sketch, "E429", {"start": v(20.01, 2.22) * mm, "end": v(19.73, 1.59) * mm});
            skLineSegment(sketch, "E430", {"start": v(11.68, 1.76) * mm, "end": v(12.09, 1.76) * mm});
            skLineSegment(sketch, "E431", {"start": v(16.16, 3.03) * mm, "end": v(16.4, 3.57) * mm});
            skLineSegment(sketch, "E432", {"start": v(-0.44, 1.12) * mm, "end": v(-0.26, 1.34) * mm});
            skLineSegment(sketch, "E433", {"start": v(17.5, -0.4) * mm, "end": v(17.23, -0.3) * mm});
            skLineSegment(sketch, "E434", {"start": v(-4.52, 4.32) * mm, "end": v(-5.07, 4.1) * mm});
            skLineSegment(sketch, "E435", {"start": v(13.65, 1.76) * mm, "end": v(13.74, 1.76) * mm});
            skLineSegment(sketch, "E436", {"start": v(10.94, 4.33) * mm, "end": v(10.39, 4.54) * mm});
            skLineSegment(sketch, "E437", {"start": v(-6.22, 3.86) * mm, "end": v(-6.82, 3.82) * mm});
            skLineSegment(sketch, "E438", {"start": v(8.98, 0.16) * mm, "end": v(8.29, 0.16) * mm});
            skLineSegment(sketch, "E439", {"start": v(11.64, 0.16) * mm, "end": v(11, 0.16) * mm});
            skLineSegment(sketch, "E440", {"start": v(-2.69, -1.8) * mm, "end": v(-2.31, -2.5) * mm});
            skLineSegment(sketch, "E441", {"start": v(7.07, 1.76) * mm, "end": v(7.63, 1.76) * mm});
            skLineSegment(sketch, "E442", {"start": v(2.42, 0.16) * mm, "end": v(1.9, 0.16) * mm});
            skLineSegment(sketch, "E443", {"start": v(6.2, 0.16) * mm, "end": v(5.53, 0.16) * mm});
            skLineSegment(sketch, "E444", {"start": v(11, 0.16) * mm, "end": v(10.34, 0.16) * mm});
            skLineSegment(sketch, "E445", {"start": v(8.29, 0.16) * mm, "end": v(7.59, 0.16) * mm});
            skLineSegment(sketch, "E446", {"start": v(-16.86, 1.9) * mm, "end": v(-16.74, 2.03) * mm});
            skLineSegment(sketch, "E447", {"start": v(9.4, 5.13) * mm, "end": v(8.96, 5.5) * mm});
            skLineSegment(sketch, "E448", {"start": v(-3.3, -1.01) * mm, "end": v(-2.69, -1.8) * mm});
            skLineSegment(sketch, "E449", {"start": v(18.26, -0.23) * mm, "end": v(18.02, -0.37) * mm});
            skLineSegment(sketch, "E450", {"start": v(16.6, 5.65) * mm, "end": v(16.53, 5.65) * mm});
            skLineSegment(sketch, "E451", {"start": v(16.53, 5.65) * mm, "end": v(16.22, 5.3) * mm});
            skLineSegment(sketch, "E452", {"start": v(-5.14, 1.63) * mm, "end": v(-4.89, 1.5) * mm});
            skLineSegment(sketch, "E453", {"start": v(-0.57, 0.88) * mm, "end": v(-0.44, 1.12) * mm});
            skLineSegment(sketch, "E454", {"start": v(9.8, 1.76) * mm, "end": v(10.3, 1.76) * mm});
            skLineSegment(sketch, "E455", {"start": v(0.2, 1.65) * mm, "end": v(0.47, 1.73) * mm});
            skLineSegment(sketch, "E456", {"start": v(13.31, 1.76) * mm, "end": v(13.5, 1.76) * mm});
            skLineSegment(sketch, "E457", {"start": v(3.34, 1.76) * mm, "end": v(3.83, 1.76) * mm});
            skLineSegment(sketch, "E458", {"start": v(15.43, 2.23) * mm, "end": v(15.83, 2.58) * mm});
            skLineSegment(sketch, "E459", {"start": v(17.22, -0.3) * mm, "end": v(16.84, -0.1) * mm});
            skLineSegment(sketch, "E460", {"start": v(-4.5, 1.11) * mm, "end": v(-4.37, 0.88) * mm});
            skLineSegment(sketch, "E461", {"start": v(15.81, -0.31) * mm, "end": v(16.25, -0.55) * mm});
            skLineSegment(sketch, "E462", {"start": v(16.55, 4.2) * mm, "end": v(16.6, 4.92) * mm});
            skLineSegment(sketch, "E463", {"start": v(15.47, 4.72) * mm, "end": v(15.02, 4.48) * mm});
            skLineSegment(sketch, "E464", {"start": v(12.26, 0.16) * mm, "end": v(11.64, 0.16) * mm});
            skLineSegment(sketch, "E465", {"start": v(19.73, 1.59) * mm, "end": v(19.4, 1.01) * mm});
            skLineSegment(sketch, "E466", {"start": v(6.51, 1.76) * mm, "end": v(7.07, 1.76) * mm});
            skLineSegment(sketch, "E467", {"start": v(3.6, 0.16) * mm, "end": v(3, 0.16) * mm});
            skLineSegment(sketch, "E468", {"start": v(7.59, 0.16) * mm, "end": v(6.9, 0.16) * mm});
            skLineSegment(sketch, "E469", {"start": v(-5.07, 4.1) * mm, "end": v(-5.64, 3.95) * mm});
            skLineSegment(sketch, "E470", {"start": v(-5.64, 3.95) * mm, "end": v(-6.22, 3.86) * mm});
            skLineSegment(sketch, "E471", {"start": v(-16.94, 1.73) * mm, "end": v(-16.86, 1.9) * mm});
            skLineSegment(sketch, "E472", {"start": v(11.54, 4.17) * mm, "end": v(10.94, 4.33) * mm});
            skLineSegment(sketch, "E473", {"start": v(-3.56, 4.93) * mm, "end": v(-4.01, 4.6) * mm});
            skLineSegment(sketch, "E474", {"start": v(8.57, 5.9) * mm, "end": v(8.22, 6.34) * mm});
            skLineSegment(sketch, "E475", {"start": v(-0.04, 1.52) * mm, "end": v(0.2, 1.65) * mm});
            skLineSegment(sketch, "E476", {"start": v(-2.8, 5.75) * mm, "end": v(-3.18, 5.31) * mm});
            skLineSegment(sketch, "E477", {"start": v(-0.65, 0.61) * mm, "end": v(-0.57, 0.88) * mm});
            skLineSegment(sketch, "E478", {"start": v(-4.26, 0.37) * mm, "end": v(-4, 0.16) * mm});
            skLineSegment(sketch, "E479", {"start": v(13.74, 1.76) * mm, "end": v(13.77, 1.76) * mm});
            skLineSegment(sketch, "E480", {"start": v(17.23, -0.3) * mm, "end": v(17.22, -0.3) * mm});
            skLineSegment(sketch, "E481", {"start": v(13.44, 4.07) * mm, "end": v(12.85, 4.04) * mm});
            skLineSegment(sketch, "E482", {"start": v(1, 1.76) * mm, "end": v(1.3, 1.76) * mm});
            skLineSegment(sketch, "E483", {"start": v(12.86, 0.16) * mm, "end": v(12.26, 0.16) * mm});
            skLineSegment(sketch, "E484", {"start": v(15.87, 5) * mm, "end": v(15.47, 4.72) * mm});
            skLineSegment(sketch, "E485", {"start": v(-5.68, 1.73) * mm, "end": v(-5.4, 1.7) * mm});
            skLineSegment(sketch, "E486", {"start": v(6.9, 0.16) * mm, "end": v(6.2, 0.16) * mm});
            skLineSegment(sketch, "E487", {"start": v(5.96, 1.76) * mm, "end": v(6.51, 1.76) * mm});
            skLineSegment(sketch, "E488", {"start": v(3, 0.16) * mm, "end": v(2.42, 0.16) * mm});
            skLineSegment(sketch, "E489", {"start": v(12.09, 1.76) * mm, "end": v(12.45, 1.76) * mm});
            skLineSegment(sketch, "E490", {"start": v(17.76, -0.43) * mm, "end": v(17.5, -0.4) * mm});
            skLineSegment(sketch, "E491", {"start": v(18.57, 0.04) * mm, "end": v(18.26, -0.23) * mm});
            skLineSegment(sketch, "E492", {"start": v(-17, 1.56) * mm, "end": v(-16.94, 1.73) * mm});
            skLineSegment(sketch, "E493", {"start": v(12.85, 4.04) * mm, "end": v(12.17, 4.08) * mm});
            skLineSegment(sketch, "E494", {"start": v(5.53, 0.16) * mm, "end": v(4.86, 0.16) * mm});
            skLineSegment(sketch, "E495", {"start": v(10.34, 0.16) * mm, "end": v(9.67, 0.16) * mm});
            skLineSegment(sketch, "E496", {"start": v(8.96, 5.5) * mm, "end": v(8.57, 5.9) * mm});
            skLineSegment(sketch, "E497", {"start": v(-8.11, 3.96) * mm, "end": v(-8.7, 4.13) * mm});
            skLineSegment(sketch, "E498", {"start": v(-3.18, 5.31) * mm, "end": v(-3.56, 4.93) * mm});
            skLineSegment(sketch, "E499", {"start": v(13.5, 1.76) * mm, "end": v(13.65, 1.76) * mm});
            skLineSegment(sketch, "E500", {"start": v(-0.68, 0.16) * mm, "end": v(-0.68, 0.33) * mm});
            skLineSegment(sketch, "E501", {"start": v(13.42, 0.16) * mm, "end": v(12.86, 0.16) * mm});
            skLineSegment(sketch, "E502", {"start": v(0.18, 0.16) * mm, "end": v(-0.11, 0.16) * mm});
            skLineSegment(sketch, "E503", {"start": v(7.63, 1.76) * mm, "end": v(8.19, 1.76) * mm});
            skLineSegment(sketch, "E504", {"start": v(5.4, 1.76) * mm, "end": v(5.96, 1.76) * mm});
            skLineSegment(sketch, "E505", {"start": v(2.02, 1.76) * mm, "end": v(2.43, 1.76) * mm});
            skLineSegment(sketch, "E506", {"start": v(14, 4.15) * mm, "end": v(13.44, 4.07) * mm});
            skLineSegment(sketch, "E507", {"start": v(-4.37, 0.88) * mm, "end": v(-4.3, 0.63) * mm});
            skLineSegment(sketch, "E508", {"start": v(10.3, 1.76) * mm, "end": v(10.79, 1.76) * mm});
            skLineSegment(sketch, "E509", {"start": v(16.84, -0.1) * mm, "end": v(16.44, 0.05) * mm});
            skLineSegment(sketch, "E510", {"start": v(16.4, 3.57) * mm, "end": v(16.55, 4.2) * mm});
            skLineSegment(sketch, "E511", {"start": v(-5.4, 1.7) * mm, "end": v(-5.14, 1.63) * mm});
            skLineSegment(sketch, "E512", {"start": v(10.39, 4.54) * mm, "end": v(9.87, 4.82) * mm});
            skLineSegment(sketch, "E513", {"start": v(18.02, -0.37) * mm, "end": v(17.76, -0.43) * mm});
            skLineSegment(sketch, "E514", {"start": v(-16.74, 2.03) * mm, "end": v(-16.6, 2.15) * mm});
            skLineSegment(sketch, "E515", {"start": v(12.78, 1.76) * mm, "end": v(13.07, 1.76) * mm});
            skLineSegment(sketch, "E516", {"start": v(-0.53, 0.16) * mm, "end": v(-0.64, 0.16) * mm});
            skLineSegment(sketch, "E517", {"start": v(0.54, 0.16) * mm, "end": v(0.18, 0.16) * mm});
            skLineSegment(sketch, "E518", {"start": v(2.87, 1.76) * mm, "end": v(3.34, 1.76) * mm});
            skLineSegment(sketch, "E519", {"start": v(11.25, 1.76) * mm, "end": v(11.68, 1.76) * mm});
            skLineSegment(sketch, "E520", {"start": v(14.87, 0.16) * mm, "end": v(14.43, 0.16) * mm});
            skLineSegment(sketch, "E521", {"start": v(8.19, 1.76) * mm, "end": v(8.74, 1.76) * mm});
            skLineSegment(sketch, "E522", {"start": v(15.6, 0.16) * mm, "end": v(15.26, 0.16) * mm});
            skLineSegment(sketch, "E523", {"start": v(12.45, 1.76) * mm, "end": v(12.78, 1.76) * mm});
            skLineSegment(sketch, "E524", {"start": v(0.94, 0.16) * mm, "end": v(0.54, 0.16) * mm});
            skLineSegment(sketch, "E525", {"start": v(0.75, 1.76) * mm, "end": v(1, 1.76) * mm});
            skLineSegment(sketch, "E526", {"start": v(4.86, 1.76) * mm, "end": v(5.4, 1.76) * mm});
            skLineSegment(sketch, "E527", {"start": v(-0.11, 0.16) * mm, "end": v(-0.35, 0.16) * mm});
            skLineSegment(sketch, "E528", {"start": v(15.26, 0.16) * mm, "end": v(14.87, 0.16) * mm});
            skLineSegment(sketch, "E529", {"start": v(9.27, 1.76) * mm, "end": v(9.8, 1.76) * mm});
            skLineSegment(sketch, "E530", {"start": v(14.4, 1.81) * mm, "end": v(14.94, 1.97) * mm});
            skLineSegment(sketch, "E531", {"start": v(0.47, 1.73) * mm, "end": v(0.75, 1.76) * mm});
            skLineSegment(sketch, "E532", {"start": v(1.3, 1.76) * mm, "end": v(1.64, 1.76) * mm});
            skLineSegment(sketch, "E533", {"start": v(-0.68, 0.33) * mm, "end": v(-0.65, 0.61) * mm});
            skLineSegment(sketch, "E534", {"start": v(13.77, 1.76) * mm, "end": v(14.4, 1.81) * mm});
            skLineSegment(sketch, "E535", {"start": v(13.07, 1.76) * mm, "end": v(13.31, 1.76) * mm});
            skLineSegment(sketch, "E536.rect.bottom", {"start": v(-23.46, -23.38) * mm, "end": v(23.46, -23.38) * mm});
            skLineSegment(sketch, "E536.rect.left", {"start": v(-23.46, -23.38) * mm, "end": v(-23.46, 23.38) * mm});
            skLineSegment(sketch, "E536.rect.right", {"start": v(23.46, -23.38) * mm, "end": v(23.46, 23.38) * mm});
            skPoint(sketch, "E536.rect.middle", {"position": v(0, 0) * mm});
            skLineSegment(sketch, "E537", {"start": v(-23.46, 23.38) * mm, "end": v(23.46, 23.38) * mm});
            skSolve(sketch);
        }
        {
            var Q0;
            Q0=makeQuery(id+"F0.imprint","IMPRINT",FACE,{"disambiguationData":[TD([[makeQuery(id+"F0.imprint","IMPRINT",EDGE,{"derivedFrom":sQuery(id+"F0.wireOp",EDGE,"E9")}),-1.0]])]});
            var Q1;
            Q1=makeQuery(id+"F0.imprint","IMPRINT",FACE,{"disambiguationData":[TD([[makeQuery(id+"F0.imprint","IMPRINT",EDGE,{"derivedFrom":sQuery(id+"F0.wireOp",EDGE,"E55")}),1.0]])]});
            var Q2;
            Q2=makeQuery(id+"F0.imprint","IMPRINT",FACE,{"disambiguationData":[TD([[makeQuery(id+"F0.imprint","IMPRINT",EDGE,{"derivedFrom":sQuery(id+"F0.wireOp",EDGE,"E70")}),-1.0]])]});
            var Q3;
            Q3=makeQuery(id+"F0.imprint","IMPRINT",FACE,{"disambiguationData":[TD([[makeQuery(id+"F0.imprint","IMPRINT",EDGE,{"derivedFrom":sQuery(id+"F0.wireOp",EDGE,"E95")}),-1.0]])]});
            var Q4;
            Q4=makeQuery(id+"F0.imprint","IMPRINT",FACE,{"disambiguationData":[TD([[makeQuery(id+"F0.imprint","IMPRINT",EDGE,{"derivedFrom":sQuery(id+"F0.wireOp",EDGE,"E143")}),1.0]])]});
            var Q5;
            Q5=makeQuery(id+"F0.imprint","IMPRINT",FACE,{"disambiguationData":[TD([[makeQuery(id+"F0.imprint","IMPRINT",EDGE,{"derivedFrom":sQuery(id+"F0.wireOp",EDGE,"E160")}),-1.0]])]});
            var Q6;
            Q6=makeQuery(id+"F0.imprint","IMPRINT",FACE,{"disambiguationData":[TD([[makeQuery(id+"F0.imprint","IMPRINT",EDGE,{"derivedFrom":sQuery(id+"F0.wireOp",EDGE,"E176")}),-1.0]])]});
            var Q7;
            Q7=makeQuery(id+"F0.imprint","IMPRINT",FACE,{"disambiguationData":[TD([[makeQuery(id+"F0.imprint","IMPRINT",EDGE,{"derivedFrom":sQuery(id+"F0.wireOp",EDGE,"E186")}),1.0]])]});
            var Q8;
            Q8=makeQuery(id+"F0.imprint","IMPRINT",FACE,{"disambiguationData":[TD([[makeQuery(id+"F0.imprint","IMPRINT",EDGE,{"derivedFrom":sQuery(id+"F0.wireOp",EDGE,"E0")}),-1.0]])]});
            var Q9;
            Q9=makeQuery(id+"F0.imprint","IMPRINT",FACE,{"disambiguationData":[TD([[makeQuery(id+"F0.imprint","IMPRINT",EDGE,{"derivedFrom":sQuery(id+"F0.wireOp",EDGE,"E2")}),-1.0]])]});
            var Q10;
            Q10=makeQuery(id+"F0.imprint","IMPRINT",FACE,{"disambiguationData":[TD([[makeQuery(id+"F0.imprint","IMPRINT",EDGE,{"derivedFrom":sQuery(id+"F0.wireOp",EDGE,"E98")}),-1.0]])]});
            var Q11;
            Q11=makeQuery(id+"F0.imprint","IMPRINT",FACE,{"disambiguationData":[TD([[makeQuery(id+"F0.imprint","IMPRINT",EDGE,{"derivedFrom":sQuery(id+"F0.wireOp",EDGE,"E0")}),1.0]])]});
            extrude(context, id + "F1", {"entities" : qUnion([Q0, Q1, Q2, Q3, Q4, Q5, Q6, Q7, Q8, Q9, Q10, Q11]), "oppositeDirection" : true, "depth" : .2 * mm});
        }
        {
            var Q0;
            Q0=makeQuery(id+"F0.imprint","IMPRINT",FACE,{"disambiguationData":[TD([[makeQuery(id+"F0.imprint","IMPRINT",EDGE,{"derivedFrom":sQuery(id+"F0.wireOp",EDGE,"E70")}),-1.0]])]});
            var Q1;
            Q1=makeQuery(id+"F0.imprint","IMPRINT",FACE,{"disambiguationData":[TD([[makeQuery(id+"F0.imprint","IMPRINT",EDGE,{"derivedFrom":sQuery(id+"F0.wireOp",EDGE,"E0")}),-1.0]])]});
            var Q2;
            Q2=makeQuery(id+"F0.imprint","IMPRINT",FACE,{"disambiguationData":[TD([[makeQuery(id+"F0.imprint","IMPRINT",EDGE,{"derivedFrom":sQuery(id+"F0.wireOp",EDGE,"E160")}),-1.0]])]});
            var Q3;
            Q3=makeQuery(id+"F0.imprint","IMPRINT",FACE,{"disambiguationData":[TD([[makeQuery(id+"F0.imprint","IMPRINT",EDGE,{"derivedFrom":sQuery(id+"F0.wireOp",EDGE,"E98")}),-1.0]])]});
            var Q4;
            Q4=makeQuery(id+"F0.imprint","IMPRINT",FACE,{"disambiguationData":[TD([[makeQuery(id+"F0.imprint","IMPRINT",EDGE,{"derivedFrom":sQuery(id+"F0.wireOp",EDGE,"E176")}),-1.0]])]});
            var Q5;
            Q5=makeQuery(id+"F0.imprint","IMPRINT",FACE,{"disambiguationData":[TD([[makeQuery(id+"F0.imprint","IMPRINT",EDGE,{"derivedFrom":sQuery(id+"F0.wireOp",EDGE,"E95")}),-1.0]])]});
            extrude(context, id + "F2", {"entities" : qUnion([Q0, Q1, Q2, Q3, Q4, Q5]), "depth" : .4 * mm});
        }
        {
            var Q0;
            Q0=makeQuery(id+"F0.imprint","IMPRINT",FACE,{"disambiguationData":[TD([[makeQuery(id+"F0.imprint","IMPRINT",EDGE,{"derivedFrom":sQuery(id+"F0.wireOp",EDGE,"E2")}),-1.0]])]});
            var Q1;
            Q1=makeQuery(id+"F0.imprint","IMPRINT",FACE,{"disambiguationData":[TD([[makeQuery(id+"F0.imprint","IMPRINT",EDGE,{"derivedFrom":sQuery(id+"F0.wireOp",EDGE,"E9")}),-1.0]])]});
            extrude(context, id + "F3", {"entities" : qUnion([Q0, Q1]), "depth" : .6 * mm});
        }
    });
